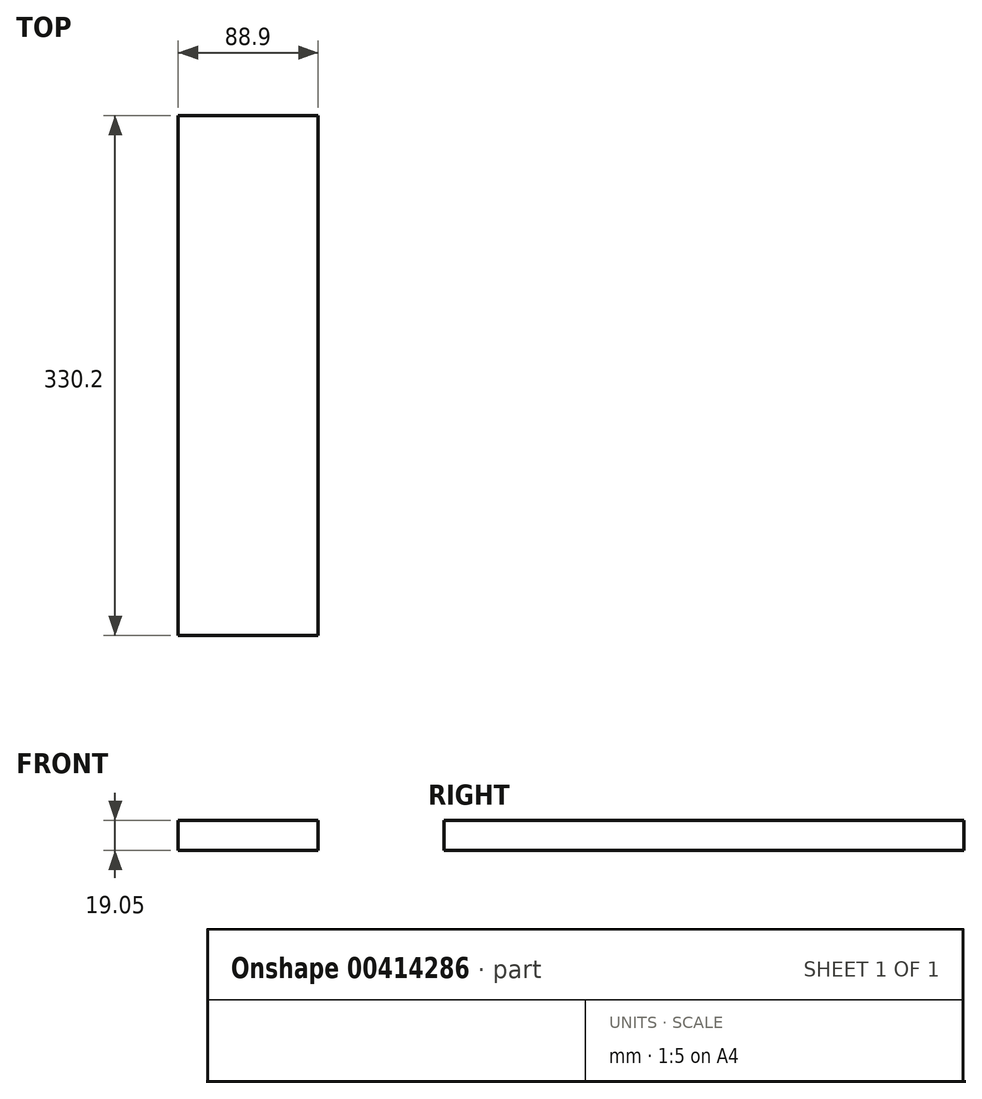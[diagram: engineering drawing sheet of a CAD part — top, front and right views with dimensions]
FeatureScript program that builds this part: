
annotation { "Feature Type Name" : "Feature", "Feature Type Description" : "" }
export const myFeature = defineFeature(function(context is Context, id is Id, definition is map)
    precondition{}
    {
        {
            var Q0;
            Q0=qCreatedBy(makeId("Front.planeOp"),FACE);
            var sketch = newSketch(context, id + "F0", { "sketchPlane" : qUnion([Q0])});
            skLineSegment(sketch, "E0.bottom", {"start": v(0, 0) * mm, "end": v(-88.9, 0) * mm});
            skLineSegment(sketch, "E0.top", {"start": v(0, 19.05) * mm, "end": v(-88.9, 19.05) * mm});
            skLineSegment(sketch, "E0.left", {"start": v(0, 0) * mm, "end": v(0, 19.05) * mm});
            skLineSegment(sketch, "E0.right", {"start": v(-88.9, 0) * mm, "end": v(-88.9, 19.05) * mm});
            skSolve(sketch);
        }
        {
            var Q0;
            Q0=qSketchRegion(id+"F0",true);
            extrude(context, id + "F1", {"entities" : qUnion([Q0]), "depth" : 330.2 * mm});
        }
    });
